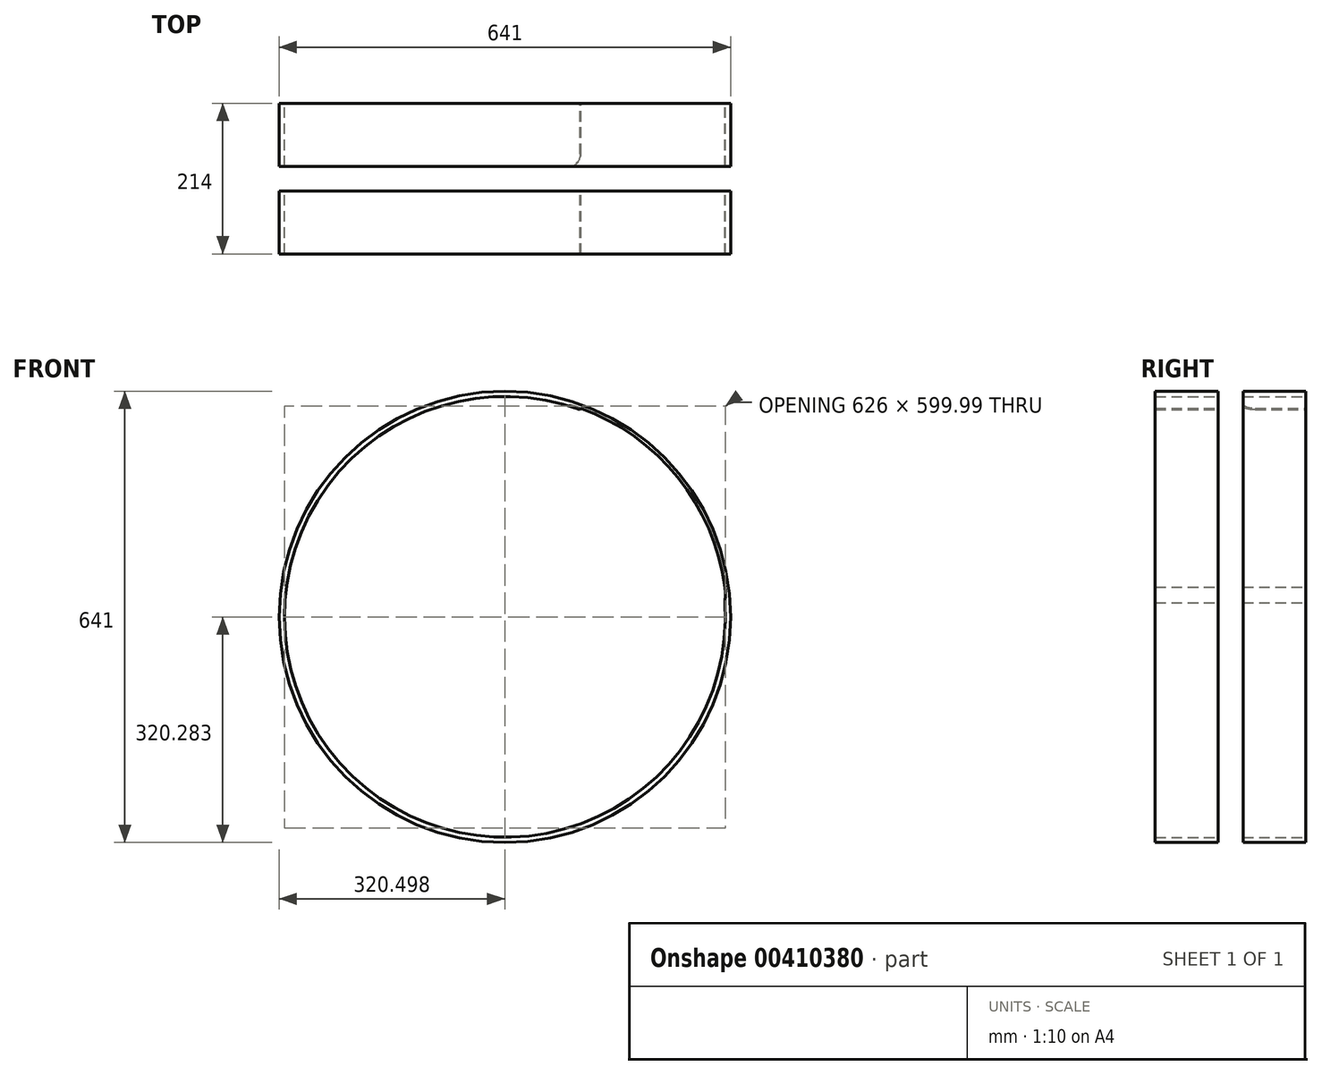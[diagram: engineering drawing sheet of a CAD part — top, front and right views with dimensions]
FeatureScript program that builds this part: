
annotation { "Feature Type Name" : "Feature", "Feature Type Description" : "" }
export const myFeature = defineFeature(function(context is Context, id is Id, definition is map)
    precondition{}
    {
        {
            var Q0;
            Q0=qCreatedBy(makeId("Front.planeOp"),FACE);
            var sketch = newSketch(context, id + "F0", { "sketchPlane" : qUnion([Q0])});
            skCircle(sketch, "E0", {"center": v(0, 0) * mm, "radius": 320.5 * mm});
            skCircle(sketch, "E1", {"center": v(0, 0) * mm, "radius": 313 * mm});
            skLineSegment(sketch, "E2", {"start": v(0, 0) * mm, "end": v(0, 370.9) * mm});
            skLineSegment(sketch, "E3", {"start": v(0, 0) * mm, "end": v(109.62, 301.17) * mm});
            skLineSegment(sketch, "E4", {"start": v(0, 0) * mm, "end": v(-109.62, 301.17) * mm});
            skLineSegment(sketch, "E5", {"start": v(-320.5, 0) * mm, "end": v(342.63, 0) * mm, "construction": true});
            skArc(sketch, "E6.0", {"start": v(312.66, 42.27) * mm, "mid": v(0, 315.5) * mm, "end": v(-312.66, 42.27) * mm});
            skPoint(sketch, "E7", {"position": v(-188, 33) * mm});
            skArc(sketch, "E8.trimOffspring", {"start": v(-312.66, 42.27) * mm, "mid": v(-312.99, 31.24) * mm, "end": v(-312.35, 20.23) * mm});
            skArc(sketch, "E9.MirrorCS", {"start": v(312.66, 42.27) * mm, "mid": v(312.99, 31.24) * mm, "end": v(312.35, 20.23) * mm});
            skSolve(sketch);
        }
        {
            var Q0;
            {var subQ0=sQuery(id+"F0.wireOp",EDGE,"E3");var subQ1=sQuery(id+"F0.wireOp",EDGE,"E0");var subQ2=makeQuery(id+"F0.imprint","INTERSECT",VERTEX,{"derivedFrom":[subQ1,subQ0]});Q0=makeQuery(id+"F0.imprint","IMPRINT",FACE,{"disambiguationData":[TD([[makeQuery(id+"F0.imprint","IMPRINT",EDGE,{"disambiguationData":[TD([[subQ2,1.0]])],"derivedFrom":subQ1}),1.0]])]});}
            var Q1;
            {var subQ0=sQuery(id+"F0.wireOp",EDGE,"E3");var subQ1=sQuery(id+"F0.wireOp",EDGE,"E0");var subQ2=makeQuery(id+"F0.imprint","INTERSECT",VERTEX,{"derivedFrom":[subQ1,subQ0]});Q1=makeQuery(id+"F0.imprint","IMPRINT",FACE,{"disambiguationData":[TD([[makeQuery(id+"F0.imprint","IMPRINT",EDGE,{"disambiguationData":[TD([[subQ2,-1.0]])],"derivedFrom":subQ1}),1.0]])]});}
            var Q2;
            {var subQ0=sQuery(id+"F0.wireOp",EDGE,"E8.trimOffspring");Q2=makeQuery(id+"F0.imprint","IMPRINT",FACE,{"disambiguationData":[TD([[makeQuery(id+"F0.imprint","IMPRINT",EDGE,{"derivedFrom":subQ0}),1.0]])]});}
            var Q3;
            {var subQ0=sQuery(id+"F0.wireOp",EDGE,"E4");var subQ1=sQuery(id+"F0.wireOp",EDGE,"E0");var subQ2=makeQuery(id+"F0.imprint","INTERSECT",VERTEX,{"derivedFrom":[subQ1,subQ0]});Q3=makeQuery(id+"F0.imprint","IMPRINT",FACE,{"disambiguationData":[TD([[makeQuery(id+"F0.imprint","IMPRINT",EDGE,{"disambiguationData":[TD([[subQ2,1.0]])],"derivedFrom":subQ1}),1.0]])]});}
            var Q4;
            {var subQ0=sQuery(id+"F0.wireOp",EDGE,"E9.MirrorCS");Q4=makeQuery(id+"F0.imprint","IMPRINT",FACE,{"disambiguationData":[TD([[makeQuery(id+"F0.imprint","IMPRINT",EDGE,{"derivedFrom":subQ0}),-1.0]])]});}
            var Q5;
            {var subQ0=sQuery(id+"F0.wireOp",EDGE,"E2");var subQ1=sQuery(id+"F0.wireOp",EDGE,"E1");var subQ2=makeQuery(id+"F0.imprint","INTERSECT",VERTEX,{"derivedFrom":[subQ1,subQ0]});Q5=makeQuery(id+"F0.imprint","IMPRINT",FACE,{"disambiguationData":[TD([[makeQuery(id+"F0.imprint","IMPRINT",EDGE,{"disambiguationData":[TD([[subQ2,-1.0]])],"derivedFrom":subQ1}),-1.0]])]});}
            var Q6;
            {var subQ0=sQuery(id+"F0.wireOp",EDGE,"E3");var subQ1=sQuery(id+"F0.wireOp",EDGE,"E1");var subQ2=makeQuery(id+"F0.imprint","INTERSECT",VERTEX,{"derivedFrom":[subQ1,subQ0]});Q6=makeQuery(id+"F0.imprint","IMPRINT",FACE,{"disambiguationData":[TD([[makeQuery(id+"F0.imprint","IMPRINT",EDGE,{"disambiguationData":[TD([[subQ2,-1.0]])],"derivedFrom":subQ1}),-1.0]])]});}
            extrude(context, id + "F1", {"entities" : qUnion([Q0, Q1, Q2, Q3, Q4, Q5, Q6]), "endBound" : BoundingType.SYMMETRIC, "depth" : 214 * mm});
        }
        {
            var Q0;
            {var subQ0=sQuery(id+"F0.wireOp",EDGE,"E4");var subQ1=sQuery(id+"F0.wireOp",EDGE,"E0");var subQ2=makeQuery(id+"F0.imprint","INTERSECT",VERTEX,{"derivedFrom":[subQ1,subQ0]});Q0=makeQuery(id+"F0.imprint","IMPRINT",FACE,{"disambiguationData":[TD([[makeQuery(id+"F0.imprint","IMPRINT",EDGE,{"disambiguationData":[TD([[subQ2,1.0]])],"derivedFrom":subQ1}),1.0]])]});}
            var Q1;
            {var subQ0=sQuery(id+"F0.wireOp",EDGE,"E3");var subQ1=sQuery(id+"F0.wireOp",EDGE,"E0");var subQ2=makeQuery(id+"F0.imprint","INTERSECT",VERTEX,{"derivedFrom":[subQ1,subQ0]});Q1=makeQuery(id+"F0.imprint","IMPRINT",FACE,{"disambiguationData":[TD([[makeQuery(id+"F0.imprint","IMPRINT",EDGE,{"disambiguationData":[TD([[subQ2,-1.0]])],"derivedFrom":subQ1}),1.0]])]});}
            var Q2;
            {var subQ0=sQuery(id+"F0.wireOp",EDGE,"E2");var subQ1=sQuery(id+"F0.wireOp",EDGE,"E1");var subQ2=makeQuery(id+"F0.imprint","INTERSECT",VERTEX,{"derivedFrom":[subQ1,subQ0]});Q2=makeQuery(id+"F0.imprint","IMPRINT",FACE,{"disambiguationData":[TD([[makeQuery(id+"F0.imprint","IMPRINT",EDGE,{"disambiguationData":[TD([[subQ2,-1.0]])],"derivedFrom":subQ1}),-1.0]])]});}
            var Q3;
            {var subQ0=sQuery(id+"F0.wireOp",EDGE,"E3");var subQ1=sQuery(id+"F0.wireOp",EDGE,"E1");var subQ2=makeQuery(id+"F0.imprint","INTERSECT",VERTEX,{"derivedFrom":[subQ1,subQ0]});Q3=makeQuery(id+"F0.imprint","IMPRINT",FACE,{"disambiguationData":[TD([[makeQuery(id+"F0.imprint","IMPRINT",EDGE,{"disambiguationData":[TD([[subQ2,-1.0]])],"derivedFrom":subQ1}),-1.0]])]});}
            var Q4;
            {var subQ0=sQuery(id+"F0.wireOp",EDGE,"E8.trimOffspring");Q4=makeQuery(id+"F0.imprint","IMPRINT",FACE,{"disambiguationData":[TD([[makeQuery(id+"F0.imprint","IMPRINT",EDGE,{"derivedFrom":subQ0}),1.0]])]});}
            var Q5;
            {var subQ0=sQuery(id+"F0.wireOp",EDGE,"E9.MirrorCS");Q5=makeQuery(id+"F0.imprint","IMPRINT",FACE,{"disambiguationData":[TD([[makeQuery(id+"F0.imprint","IMPRINT",EDGE,{"derivedFrom":subQ0}),-1.0]])]});}
            extrude(context, id + "F2", {"entities" : qUnion([Q0, Q1, Q2, Q3, Q4, Q5]), "operationType" : NewBodyOperationType.REMOVE, "endBound" : BoundingType.SYMMETRIC, "depth" : 35 * mm});
        }
        {
            var Q0;
            Q0=makeQuery(id+"F2.boolean.opBoolean","COPY",EDGE,{"derivedFrom":makeQuery(id+"F2.opExtrude","CAP_EDGE",EDGE,{"disambiguationData":[OSD([sQuery(id+"F0.wireOp",EDGE,"E4")])],"isStart":true})});
            var Q1;
            Q1=makeQuery(id+"F2.boolean.opBoolean","COPY",EDGE,{"derivedFrom":makeQuery(id+"F2.opExtrude","CAP_EDGE",EDGE,{"disambiguationData":[OSD([sQuery(id+"F0.wireOp",EDGE,"E3")])],"isStart":true})});
            var Q2;
            Q2=makeQuery(id+"F2.boolean.opBoolean","COPY",EDGE,{"derivedFrom":makeQuery(id+"F2.opExtrude","CAP_EDGE",EDGE,{"disambiguationData":[OSD([sQuery(id+"F0.wireOp",EDGE,"E4")])],"isStart":false})});
            var Q3;
            Q3=makeQuery(id+"F2.boolean.opBoolean","COPY",EDGE,{"derivedFrom":makeQuery(id+"F2.opExtrude","CAP_EDGE",EDGE,{"disambiguationData":[OSD([sQuery(id+"F0.wireOp",EDGE,"E3")])],"isStart":false})});
            fillet(context, id + "F3", {"entities" : qUnion([Q0, Q1, Q2, Q3]), "radius" : 17.5 * mm, "tangentPropagation" : true, "allowEdgeOverflow" : false});
        }
    });
